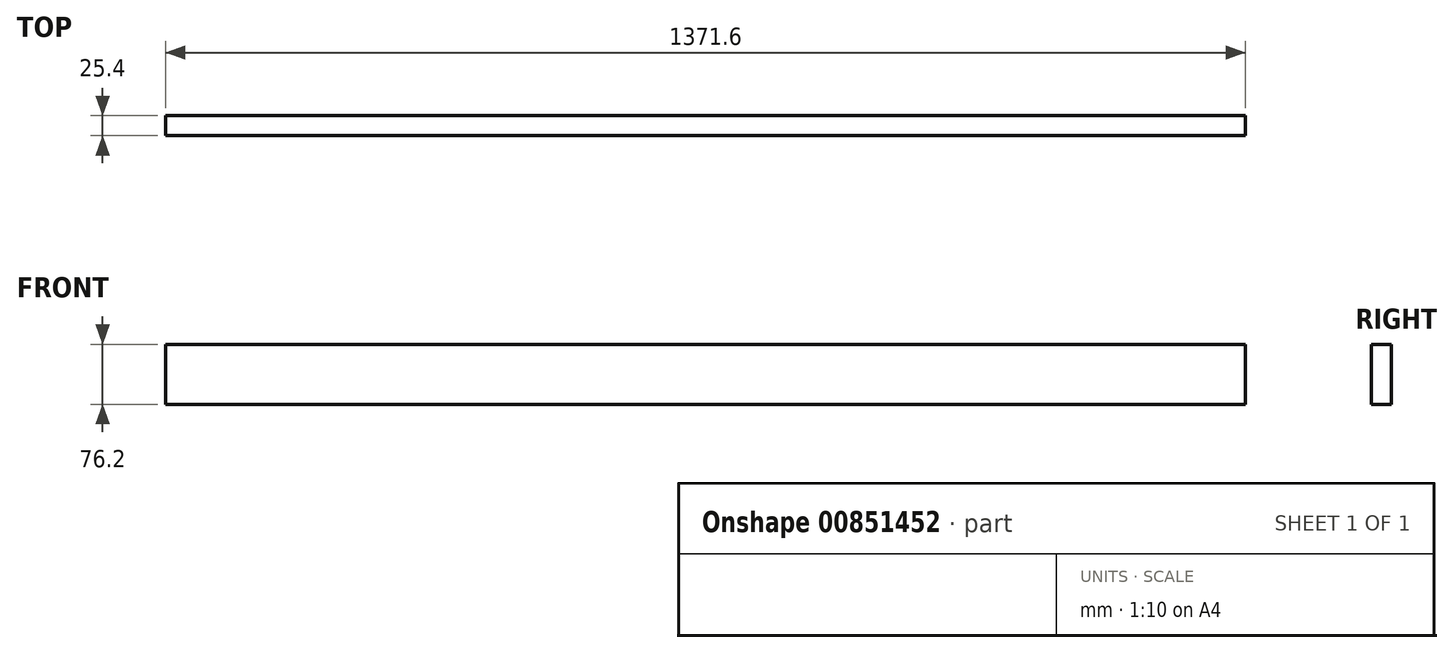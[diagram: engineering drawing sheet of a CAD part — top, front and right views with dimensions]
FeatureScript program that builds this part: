
annotation { "Feature Type Name" : "Feature", "Feature Type Description" : "" }
export const myFeature = defineFeature(function(context is Context, id is Id, definition is map)
    precondition{}
    {
        {
            var Q0;
            Q0=qCreatedBy(makeId("Front.planeOp"),FACE);
            var sketch = newSketch(context, id + "F0", { "sketchPlane" : qUnion([Q0])});
            skLineSegment(sketch, "E0.bottom", {"start": v(-678.86, -32.5) * mm, "end": v(692.74, -32.5) * mm});
            skLineSegment(sketch, "E0.top", {"start": v(-678.86, -108.7) * mm, "end": v(692.74, -108.7) * mm});
            skLineSegment(sketch, "E0.left", {"start": v(-678.86, -32.5) * mm, "end": v(-678.86, -108.7) * mm});
            skLineSegment(sketch, "E0.right", {"start": v(692.74, -32.5) * mm, "end": v(692.74, -108.7) * mm});
            skSolve(sketch);
        }
        {
            var Q0;
            Q0 = qSketchRegion(id + "F0", true);
            extrude(context, id + "F1", {"entities" : qUnion([Q0]), "depth" : 25.4 * mm, "offsetDistance" : 25.4 * mm});
        }
    });
